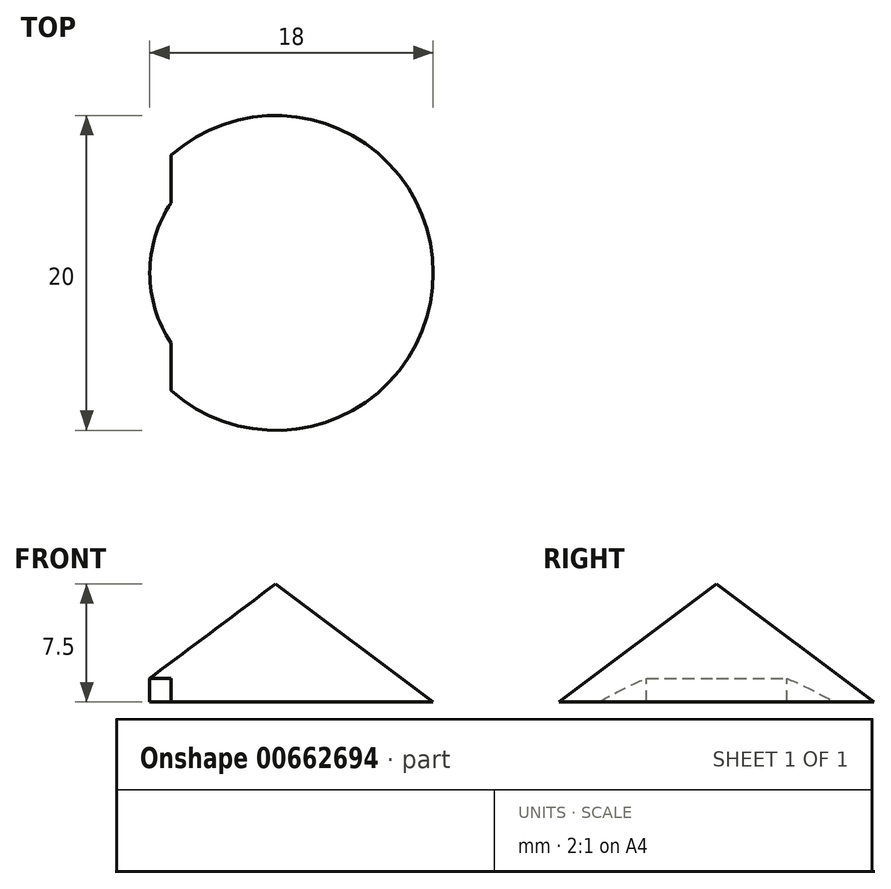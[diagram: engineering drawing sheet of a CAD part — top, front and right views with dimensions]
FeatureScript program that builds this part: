
annotation { "Feature Type Name" : "Feature", "Feature Type Description" : "" }
export const myFeature = defineFeature(function(context is Context, id is Id, definition is map)
    precondition{}
    {
        {
            var Q0;
            Q0=qCreatedBy(makeId("Front.planeOp"),FACE);
            var sketch = newSketch(context, id + "F0", { "sketchPlane" : qUnion([Q0])});
            skLineSegment(sketch, "E0", {"start": v(0, 30) * mm, "end": v(0, 37.5) * mm});
            skLineSegment(sketch, "E1", {"start": v(0, 37.5) * mm, "end": v(10, 30) * mm});
            skLineSegment(sketch, "E2", {"start": v(10, 30) * mm, "end": v(0, 30) * mm});
            skPoint(sketch, "E3.end.orphan", {"position": v(10, 0) * mm});
            skSolve(sketch);
        }
        {
            var Q0;
            Q0=qSketchRegion(id+"F0",true);
            var Q1;
            Q1=sQuery(id+"F0.wireOp",EDGE,"E0");
            revolve(context, id + "F1", {"entities" : qUnion([Q0]), "axis" : qUnion([Q1]), "revolveType" : RevolveType.FULL});
        }
        {
            var Q0;
            Q0=qCreatedBy(makeId("Top.planeOp"),FACE);
            var sketch = newSketch(context, id + "F2", { "sketchPlane" : qUnion([Q0])});
            skLineSegment(sketch, "E4", {"start": v(-6.64, 7.5) * mm, "end": v(-6.64, -9.07) * mm});
            skLineSegment(sketch, "E5", {"start": v(-6.64, -9.07) * mm, "end": v(-11.55, -9.07) * mm});
            skLineSegment(sketch, "E6", {"start": v(-11.55, -9.07) * mm, "end": v(-11.55, 7.5) * mm});
            skLineSegment(sketch, "E7", {"start": v(-11.55, 7.5) * mm, "end": v(-6.64, 7.5) * mm});
            skCircle(sketch, "E8", {"center": v(0, 0) * mm, "radius": 8 * mm});
            skLineSegment(sketch, "E9", {"start": v(10.46, -5.33) * mm, "end": v(-3.95, -10.95) * mm});
            skLineSegment(sketch, "E10.MirrorCS", {"start": v(10.46, 5.33) * mm, "end": v(-3.95, 10.95) * mm});
            skSolve(sketch);
        }
        {
            var Q0;
            {var subQ0=sQuery(id+"F2.wireOp",EDGE,"E5");Q0=makeQuery(id+"F2.imprint","IMPRINT",FACE,{"disambiguationData":[TD([[makeQuery(id+"F2.imprint","IMPRINT",EDGE,{"derivedFrom":subQ0}),-1.0]])]});}
            var Q1;
            {var subQ0=sQuery(id+"F2.wireOp",EDGE,"E8");var subQ1=sQuery(id+"F2.wireOp",EDGE,"E4");var subQ2=makeQuery(id+"F2.imprint","INTERSECT",VERTEX,{"disambiguationData":[OD(0.0)],"derivedFrom":[subQ1,subQ0]});Q1=makeQuery(id+"F2.imprint","IMPRINT",FACE,{"disambiguationData":[TD([[makeQuery(id+"F2.imprint","IMPRINT",EDGE,{"disambiguationData":[TD([[subQ2,-1.0]])],"derivedFrom":subQ1}),-1.0]])]});}
            extrude(context, id + "F3", {"entities" : qUnion([Q0, Q1]), "operationType" : NewBodyOperationType.REMOVE, "oppositeDirection" : true, "depth" : 5 * mm, "offsetDistance" : 25 * mm, "hasSecondDirection" : true, "secondDirectionOppositeDirection" : false, "secondDirectionDepth" : 50 * mm});
        }
        {
            var Q0;
            {var subQ0=sQuery(id+"F2.wireOp",EDGE,"E8");var subQ1=sQuery(id+"F2.wireOp",EDGE,"E4");var subQ2=makeQuery(id+"F2.imprint","INTERSECT",VERTEX,{"disambiguationData":[OD(0.0)],"derivedFrom":[subQ1,subQ0]});Q0=makeQuery(id+"F2.imprint","IMPRINT",FACE,{"disambiguationData":[TD([[makeQuery(id+"F2.imprint","IMPRINT",EDGE,{"disambiguationData":[TD([[subQ2,-1.0]])],"derivedFrom":subQ1}),1.0]])]});}
            var Q1;
            {var subQ0=sQuery(id+"F2.wireOp",EDGE,"E9");var subQ1=sQuery(id+"F2.wireOp",EDGE,"E8");var subQ2=makeQuery(id+"F2.imprint","INTERSECT",VERTEX,{"disambiguationData":[OD(0.0)],"derivedFrom":[subQ1,subQ0]});Q1=makeQuery(id+"F2.imprint","IMPRINT",FACE,{"disambiguationData":[TD([[makeQuery(id+"F2.imprint","IMPRINT",EDGE,{"disambiguationData":[TD([[subQ2,-1.0]])],"derivedFrom":subQ1}),1.0]])]});}
            extrude(context, id + "F4", {"entities" : qUnion([Q0, Q1]), "operationType" : NewBodyOperationType.REMOVE, "depth" : 30 * mm, "offsetDistance" : 25 * mm});
        }
        {
            var Q0;
            Q0=sQuery(id+"F2.wireOp",EDGE,"E9");
            cPlane(context, id + "F5", {"entities" : qUnion([Q0]), "cplaneType" : CPlaneType.LINE_ANGLE, "offset" : 25 * mm, "angle" : 180 * degree, "width" : 150 * mm, "height" : 150 * mm});
        }
        {
            var Q0;
            Q0=qCreatedBy(id+"F5.planeOp",FACE);
            var sketch = newSketch(context, id + "F6", { "sketchPlane" : qUnion([Q0])});
            skArc(sketch, "E11", {"start": v(0, 2) * mm, "mid": v(4.03, 15) * mm, "end": v(0, 28) * mm});
            skArc(sketch, "E12", {"start": v(0, 28) * mm, "mid": v(-4.03, 15) * mm, "end": v(0, 2) * mm});
            skSolve(sketch);
        }
        {
            var Q0;
            Q0=qSketchRegion(id+"F6",true);
            extrude(context, id + "F7", {"entities" : qUnion([Q0]), "operationType" : NewBodyOperationType.REMOVE, "depth" : 5 * mm, "offsetDistance" : 25 * mm, "hasSecondDirection" : true, "secondDirectionOppositeDirection" : true, "secondDirectionDepth" : 5 * mm});
        }
        {
            var Q0;
            Q0=sQuery(id+"F2.wireOp",EDGE,"E10.MirrorCS");
            cPlane(context, id + "F8", {"entities" : qUnion([Q0]), "cplaneType" : CPlaneType.LINE_ANGLE, "offset" : 25 * mm, "angle" : 0 * degree, "width" : 150 * mm, "height" : 150 * mm});
        }
        {
            var Q0;
            Q0=qCreatedBy(id+"F8.planeOp",FACE);
            var sketch = newSketch(context, id + "F9", { "sketchPlane" : qUnion([Q0])});
            skArc(sketch, "E13", {"start": v(0, 2) * mm, "mid": v(4.03, 15) * mm, "end": v(0, 28) * mm});
            skArc(sketch, "E14", {"start": v(0, 28) * mm, "mid": v(-4.03, 15) * mm, "end": v(0, 2) * mm});
            skSolve(sketch);
        }
        {
            var Q0;
            Q0=qSketchRegion(id+"F9",true);
            extrude(context, id + "F10", {"entities" : qUnion([Q0]), "operationType" : NewBodyOperationType.REMOVE, "oppositeDirection" : true, "depth" : 5 * mm, "offsetDistance" : 25 * mm, "hasSecondDirection" : true, "secondDirectionOppositeDirection" : false, "secondDirectionDepth" : 5 * mm});
        }
        {
            var Q0;
            Q0=qCreatedBy(makeId("Right.planeOp"),FACE);
            var sketch = newSketch(context, id + "F11", { "sketchPlane" : qUnion([Q0])});
            skArc(sketch, "E15", {"start": v(0, 2) * mm, "mid": v(4.03, 15) * mm, "end": v(0, 28) * mm});
            skArc(sketch, "E16", {"start": v(0, 28) * mm, "mid": v(-4.03, 15) * mm, "end": v(0, 2) * mm});
            skSolve(sketch);
        }
        {
            var Q0;
            Q0=qSketchRegion(id+"F11",true);
            extrude(context, id + "F12", {"entities" : qUnion([Q0]), "operationType" : NewBodyOperationType.REMOVE, "depth" : 20 * mm, "offsetDistance" : 25 * mm});
        }
    });
